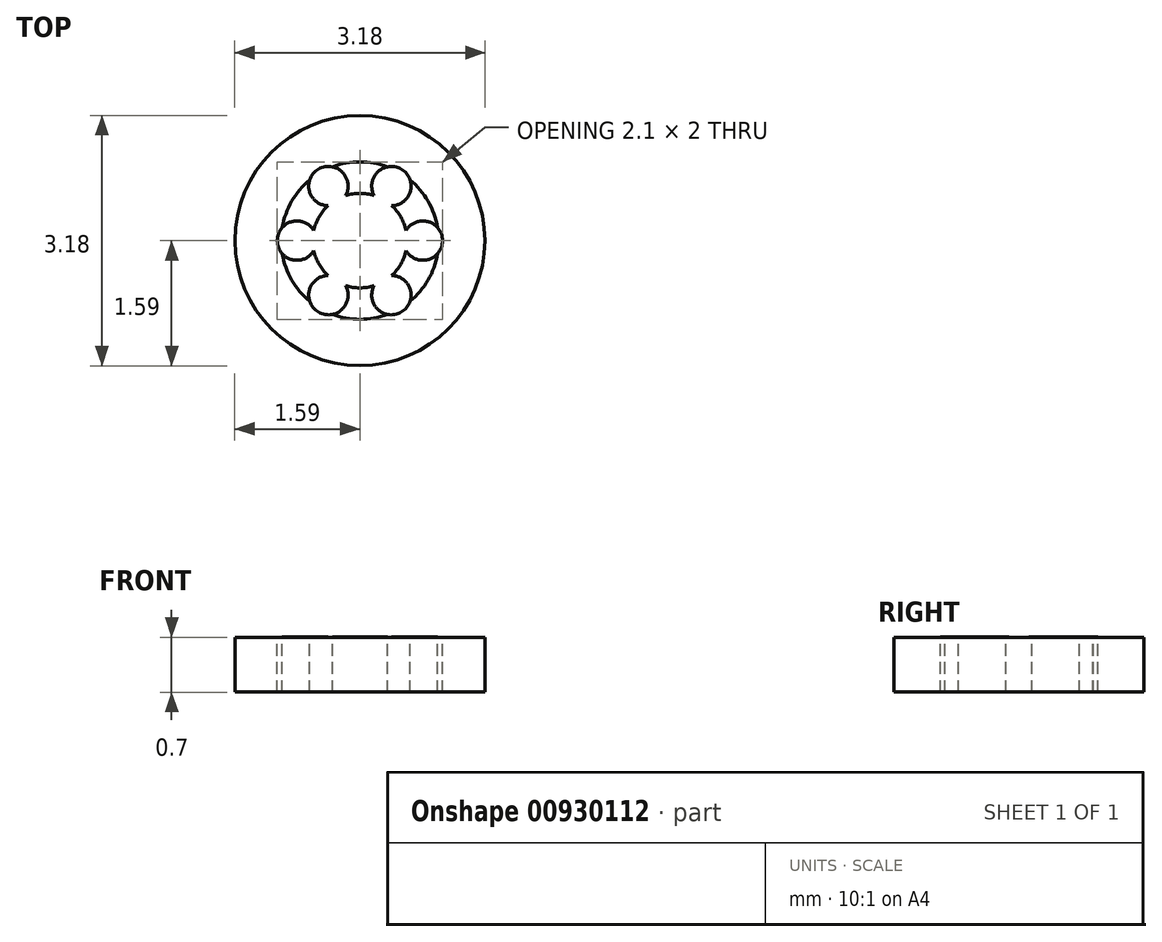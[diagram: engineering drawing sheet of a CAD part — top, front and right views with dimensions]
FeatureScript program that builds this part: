
annotation { "Feature Type Name" : "Feature", "Feature Type Description" : "" }
export const myFeature = defineFeature(function(context is Context, id is Id, definition is map)
    precondition{}
    {
        {
            var Q0;
            Q0=qCreatedBy(makeId("Top.planeOp"),FACE);
            var sketch = newSketch(context, id + "F0", { "sketchPlane" : qUnion([Q0])});
            skCircle(sketch, "E0", {"center": v(0, 0) * mm, "radius": 0.6 * mm});
            skCircle(sketch, "E1", {"center": v(0, 0) * mm, "radius": 1.59 * mm});
            skCircle(sketch, "E2", {"center": v(0.8, 0) * mm, "radius": 0.25 * mm});
            skCircle(sketch, "E3.1.0", {"center": v(0.4, 0.7) * mm, "radius": 0.25 * mm});
            skCircle(sketch, "E3.2.0", {"center": v(-0.4, 0.7) * mm, "radius": 0.25 * mm});
            skCircle(sketch, "E3.3.0", {"center": v(-0.8, 0) * mm, "radius": 0.25 * mm});
            skCircle(sketch, "E3.4.0", {"center": v(-0.4, -0.7) * mm, "radius": 0.25 * mm});
            skCircle(sketch, "E3.5.0", {"center": v(0.4, -0.7) * mm, "radius": 0.25 * mm});
            skCircle(sketch, "E4", {"center": v(0, 0) * mm, "radius": 1 * mm});
            skSolve(sketch);
        }
        {
            var Q0;
            {var subQ0=sQuery(id+"F0.wireOp",EDGE,"E3.2.0");var subQ1=sQuery(id+"F0.wireOp",EDGE,"E0");var subQ2=makeQuery(id+"F0.imprint","INTERSECT",VERTEX,{"disambiguationData":[OD(1.0)],"derivedFrom":[subQ1,subQ0]});Q0=makeQuery(id+"F0.imprint","IMPRINT",FACE,{"disambiguationData":[TD([[makeQuery(id+"F0.imprint","IMPRINT",EDGE,{"disambiguationData":[TD([[subQ2,-1.0]])],"derivedFrom":subQ1}),-1.0]])]});}
            var Q1;
            {var subQ0=sQuery(id+"F0.wireOp",EDGE,"E3.1.0");var subQ1=sQuery(id+"F0.wireOp",EDGE,"E0");var subQ2=makeQuery(id+"F0.imprint","INTERSECT",VERTEX,{"disambiguationData":[OD(1.0)],"derivedFrom":[subQ1,subQ0]});Q1=makeQuery(id+"F0.imprint","IMPRINT",FACE,{"disambiguationData":[TD([[makeQuery(id+"F0.imprint","IMPRINT",EDGE,{"disambiguationData":[TD([[subQ2,-1.0]])],"derivedFrom":subQ1}),-1.0]])]});}
            var Q2;
            {var subQ0=sQuery(id+"F0.wireOp",EDGE,"E3.1.0");var subQ1=sQuery(id+"F0.wireOp",EDGE,"E0");var subQ2=makeQuery(id+"F0.imprint","INTERSECT",VERTEX,{"disambiguationData":[OD(0.0)],"derivedFrom":[subQ1,subQ0]});Q2=makeQuery(id+"F0.imprint","IMPRINT",FACE,{"disambiguationData":[TD([[makeQuery(id+"F0.imprint","IMPRINT",EDGE,{"disambiguationData":[TD([[subQ2,1.0]])],"derivedFrom":subQ1}),-1.0]])]});}
            var Q3;
            {var subQ0=sQuery(id+"F0.wireOp",EDGE,"E3.5.0");var subQ1=sQuery(id+"F0.wireOp",EDGE,"E0");var subQ2=makeQuery(id+"F0.imprint","INTERSECT",VERTEX,{"disambiguationData":[OD(1.0)],"derivedFrom":[subQ1,subQ0]});Q3=makeQuery(id+"F0.imprint","IMPRINT",FACE,{"disambiguationData":[TD([[makeQuery(id+"F0.imprint","IMPRINT",EDGE,{"disambiguationData":[TD([[subQ2,-1.0]])],"derivedFrom":subQ1}),-1.0]])]});}
            var Q4;
            {var subQ0=sQuery(id+"F0.wireOp",EDGE,"E3.4.0");var subQ1=sQuery(id+"F0.wireOp",EDGE,"E0");var subQ2=makeQuery(id+"F0.imprint","INTERSECT",VERTEX,{"disambiguationData":[OD(1.0)],"derivedFrom":[subQ1,subQ0]});Q4=makeQuery(id+"F0.imprint","IMPRINT",FACE,{"disambiguationData":[TD([[makeQuery(id+"F0.imprint","IMPRINT",EDGE,{"disambiguationData":[TD([[subQ2,-1.0]])],"derivedFrom":subQ1}),-1.0]])]});}
            var Q5;
            {var subQ0=sQuery(id+"F0.wireOp",EDGE,"E3.3.0");var subQ1=sQuery(id+"F0.wireOp",EDGE,"E0");var subQ2=makeQuery(id+"F0.imprint","INTERSECT",VERTEX,{"disambiguationData":[OD(1.0)],"derivedFrom":[subQ1,subQ0]});Q5=makeQuery(id+"F0.imprint","IMPRINT",FACE,{"disambiguationData":[TD([[makeQuery(id+"F0.imprint","IMPRINT",EDGE,{"disambiguationData":[TD([[subQ2,-1.0]])],"derivedFrom":subQ1}),-1.0]])]});}
            extrude(context, id + "F1", {"entities" : qUnion([Q0, Q1, Q2, Q3, Q4, Q5]), "depth" : 1 / 203.2 * mm, "offsetDistance" : 25 * mm});
        }
        {
            var Q0;
            Q0=makeQuery(id+"F0.imprint","IMPRINT",FACE,{"disambiguationData":[TD([[makeQuery(id+"F0.imprint","IMPRINT",EDGE,{"derivedFrom":sQuery(id+"F0.wireOp",EDGE,"E1")}),1.0]])]});
            extrude(context, id + "F2", {"entities" : qUnion([Q0]), "operationType" : NewBodyOperationType.ADD, "depth" : 1 / 203.2 * mm - .7 * mm, "offsetDistance" : 25 * mm});
        }
    });
